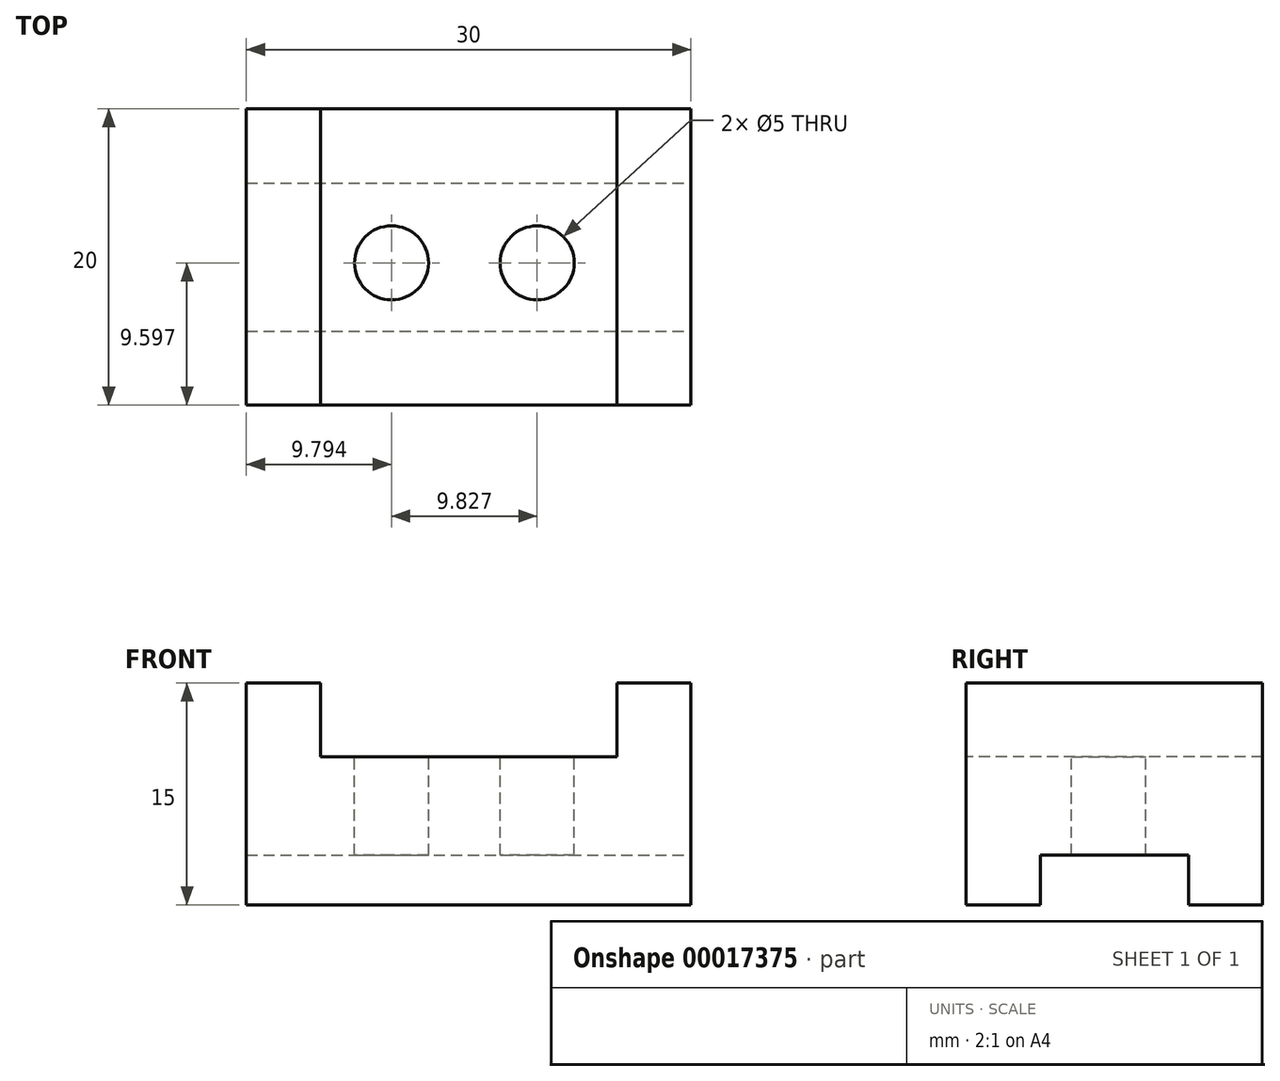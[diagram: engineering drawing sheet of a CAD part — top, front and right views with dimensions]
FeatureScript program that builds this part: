
annotation { "Feature Type Name" : "Feature", "Feature Type Description" : "" }
export const myFeature = defineFeature(function(context is Context, id is Id, definition is map)
    precondition{}
    {
        {
            var Q0;
            Q0=qCreatedBy(makeId("Right.planeOp"),FACE);
            var sketch = newSketch(context, id + "F0", { "sketchPlane" : qUnion([Q0])});
            skLineSegment(sketch, "E0", {"start": v(-13.5, 3.84) * mm, "end": v(-13.5, -6.16) * mm});
            skLineSegment(sketch, "E1", {"start": v(-13.5, -6.16) * mm, "end": v(-8.5, -6.16) * mm});
            skLineSegment(sketch, "E2", {"start": v(-8.5, -6.16) * mm, "end": v(-8.5, -2.78) * mm});
            skLineSegment(sketch, "E3", {"start": v(-8.5, -2.78) * mm, "end": v(1.5, -2.78) * mm});
            skLineSegment(sketch, "E4", {"start": v(1.5, -2.78) * mm, "end": v(1.5, -6.16) * mm});
            skLineSegment(sketch, "E5", {"start": v(1.5, -6.16) * mm, "end": v(6.5, -6.16) * mm});
            skLineSegment(sketch, "E6", {"start": v(6.5, -6.16) * mm, "end": v(6.5, 3.84) * mm});
            skLineSegment(sketch, "E7", {"start": v(6.5, 3.84) * mm, "end": v(-13.5, 3.84) * mm});
            skSolve(sketch);
        }
        {
            var Q0;
            Q0=makeQuery(id+"F0.imprint","IMPRINT",FACE,{"disambiguationData":[TD([[makeQuery(id+"F0.imprint","IMPRINT",EDGE,{"derivedFrom":sQuery(id+"F0.wireOp",EDGE,"E0")}),1.0]])]});
            extrude(context, id + "F1", {"entities" : qUnion([Q0]), "oppositeDirection" : true, "depth" : 30 * mm});
        }
        {
            var Q0;
            Q0=makeQuery(id+"F1.opExtrude","SWEPT_FACE",FACE,{"disambiguationData":[OSD([sQuery(id+"F0.wireOp",EDGE,"E7")])]});
            var sketch = newSketch(context, id + "F2", { "sketchPlane" : qUnion([Q0])});
            skLineSegment(sketch, "E8.bottom", {"start": v(-30, 6.5) * mm, "end": v(-25, 6.5) * mm});
            skLineSegment(sketch, "E8.top", {"start": v(-30, -13.5) * mm, "end": v(-25, -13.5) * mm});
            skLineSegment(sketch, "E8.left", {"start": v(-30, 6.5) * mm, "end": v(-30, -13.5) * mm});
            skLineSegment(sketch, "E8.right", {"start": v(-25, 6.5) * mm, "end": v(-25, -13.5) * mm});
            skLineSegment(sketch, "E9.bottom", {"start": v(0, 6.5) * mm, "end": v(-5, 6.5) * mm});
            skLineSegment(sketch, "E9.top", {"start": v(0, -13.5) * mm, "end": v(-5, -13.5) * mm});
            skLineSegment(sketch, "E9.left", {"start": v(0, 6.5) * mm, "end": v(0, -13.5) * mm});
            skLineSegment(sketch, "E9.right", {"start": v(-5, 6.5) * mm, "end": v(-5, -13.5) * mm});
            skSolve(sketch);
        }
        {
            var Q0;
            Q0=makeQuery(id+"F2.imprint","IMPRINT",FACE,{"disambiguationData":[TD([[makeQuery(id+"F2.imprint","IMPRINT",EDGE,{"derivedFrom":sQuery(id+"F2.wireOp",EDGE,"E8.bottom")}),-1.0]])]});
            extrude(context, id + "F3", {"entities" : qUnion([Q0]), "operationType" : NewBodyOperationType.ADD, "depth" : 5 * mm});
        }
        {
            var Q0;
            Q0=makeQuery(id+"F2.imprint","IMPRINT",FACE,{"disambiguationData":[TD([[makeQuery(id+"F2.imprint","IMPRINT",EDGE,{"derivedFrom":sQuery(id+"F2.wireOp",EDGE,"E9.bottom")}),-1.0]])]});
            extrude(context, id + "F4", {"entities" : qUnion([Q0]), "operationType" : NewBodyOperationType.ADD, "depth" : 5 * mm});
        }
        {
            var Q0;
            {var subQ3=sQuery(id+"F2.wireOp",EDGE,"E8.right");Q0=makeQuery(id+"F2.imprint","IMPRINT",FACE,{"disambiguationData":[TD([[makeQuery(id+"F2.imprint","IMPRINT",EDGE,{"derivedFrom":subQ3}),1.0]])]});}
            var sketch = newSketch(context, id + "F5", { "sketchPlane" : qUnion([Q0])});
            skCircle(sketch, "E10", {"center": v(-20.2, -3.9) * mm, "radius": 2.5 * mm});
            skCircle(sketch, "E11", {"center": v(-10.38, -3.9) * mm, "radius": 2.5 * mm});
            skSolve(sketch);
        }
        {
            var Q0;
            Q0=sQuery(id+"F5.wireOp",VERTEX,"E10.center");
            var Q1;
            Q1=makeQuery(id+"F1.opExtrude","SWEPT_BODY",BODY,{"disambiguationData":[OSD([sQuery(id+"F0.wireOp",EDGE,"E0"),sQuery(id+"F0.wireOp",EDGE,"E1"),sQuery(id+"F0.wireOp",EDGE,"E2"),sQuery(id+"F0.wireOp",EDGE,"E3"),sQuery(id+"F0.wireOp",EDGE,"E4"),sQuery(id+"F0.wireOp",EDGE,"E5"),sQuery(id+"F0.wireOp",EDGE,"E6"),sQuery(id+"F0.wireOp",EDGE,"E7")])]});
            hole(context, id + "F6", {"style" : HoleStyle.SIMPLE, "holeDiameter" : 5 * mm, "endStyle" : HoleEndStyle.THROUGH, "locations" : qUnion([Q0]), "scope" : qUnion([Q1])});
        }
        {
            var Q0;
            Q0=sQuery(id+"F5.wireOp",VERTEX,"E11.center");
            var Q1;
            Q1=makeQuery(id+"F1.opExtrude","SWEPT_BODY",BODY,{"disambiguationData":[OSD([sQuery(id+"F0.wireOp",EDGE,"E0"),sQuery(id+"F0.wireOp",EDGE,"E1"),sQuery(id+"F0.wireOp",EDGE,"E2"),sQuery(id+"F0.wireOp",EDGE,"E3"),sQuery(id+"F0.wireOp",EDGE,"E4"),sQuery(id+"F0.wireOp",EDGE,"E5"),sQuery(id+"F0.wireOp",EDGE,"E6"),sQuery(id+"F0.wireOp",EDGE,"E7")])]});
            hole(context, id + "F7", {"style" : HoleStyle.SIMPLE, "holeDiameter" : 5 * mm, "endStyle" : HoleEndStyle.THROUGH, "locations" : qUnion([Q0]), "scope" : qUnion([Q1])});
        }
    });
